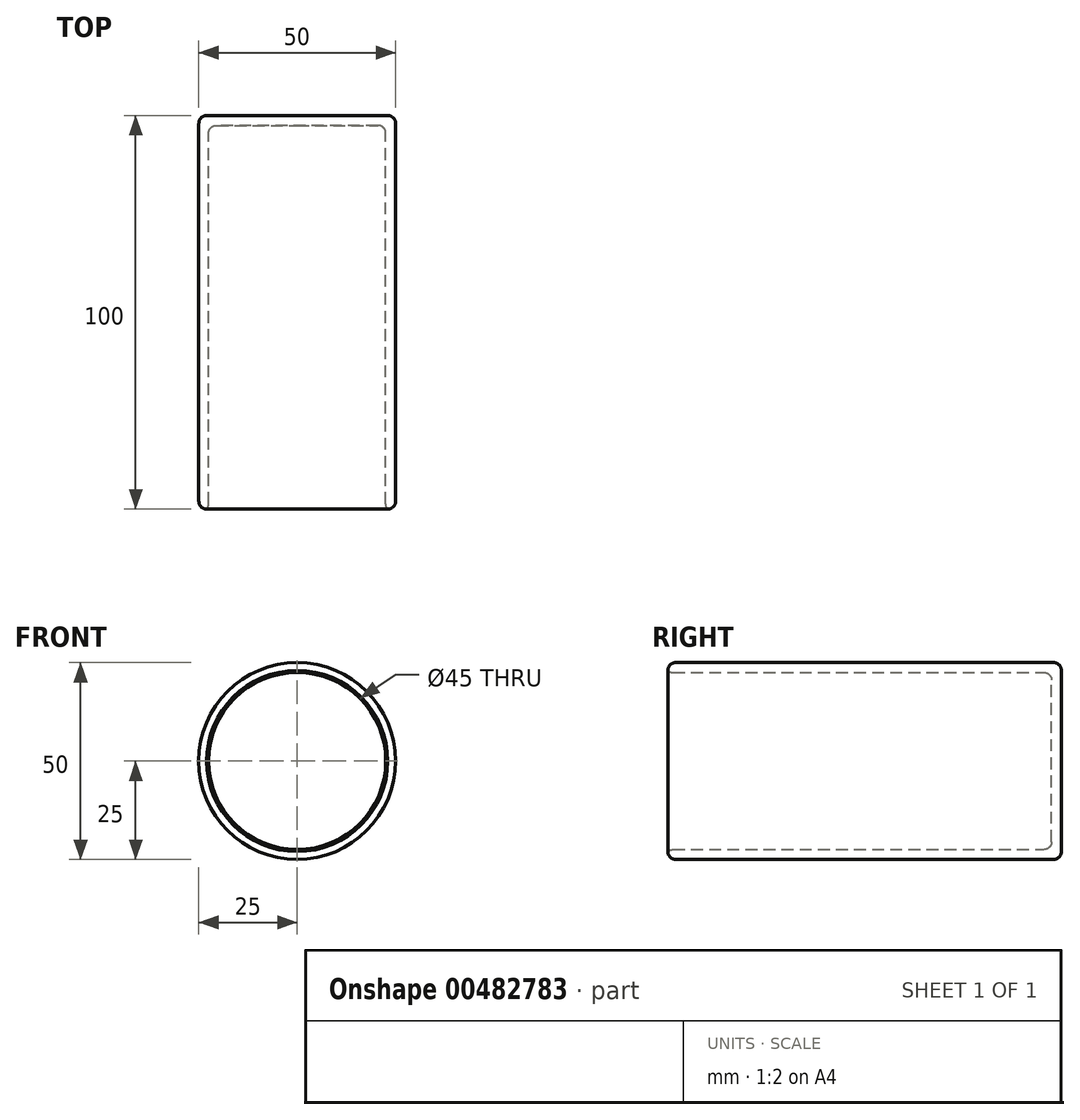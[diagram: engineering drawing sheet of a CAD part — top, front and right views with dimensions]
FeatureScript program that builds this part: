
annotation { "Feature Type Name" : "Feature", "Feature Type Description" : "" }
export const myFeature = defineFeature(function(context is Context, id is Id, definition is map)
    precondition{}
    {
        {
            var Q0;
            Q0=qCreatedBy(makeId("Front.planeOp"),FACE);
            var sketch = newSketch(context, id + "F0", { "sketchPlane" : qUnion([Q0])});
            skCircle(sketch, "E0", {"center": v(0, 0) * mm, "radius": 25 * mm});
            skSolve(sketch);
        }
        {
            var Q0;
            Q0 = qSketchRegion(id + "F0", true);
            extrude(context, id + "F1", {"entities" : qUnion([Q0]), "depth" : 100 * mm});
        }
        {
            var Q0;
            Q0=makeQuery(id+"F1.opExtrude","CAP_FACE",FACE,{"disambiguationData":[OSD([sQuery(id+"F0.wireOp",EDGE,"E0")])],"isStart":false});
            shell(context, id + "F2", {"entities" : qUnion([Q0]), "thickness" : 2.5 * mm});
        }
        {
            var Q0;
            Q0=makeQuery(id+"F1.opExtrude","SWEPT_FACE",FACE,{"disambiguationData":[OSD([sQuery(id+"F0.wireOp",EDGE,"E0")])]});
            fillet(context, id + "F3", {"entities" : qUnion([Q0]), "radius" : 2 * mm, "tangentPropagation" : true, "allowEdgeOverflow" : false});
        }
        {
            var Q0;
            {var subQ0=sQuery(id+"F0.wireOp",EDGE,"E0");Q0=makeQuery(id+"F2.opShell","OFFSET_FACE",FACE,{"disambiguationData":[OSD([subQ0]),TDD([makeQuery(id+"F1.opExtrude","SWEPT_FACE",FACE,{"disambiguationData":[OSD([subQ0])]})])]});}
            fillet(context, id + "F4", {"entities" : qUnion([Q0]), "radius" : 2 * mm, "tangentPropagation" : true, "allowEdgeOverflow" : false});
        }
    });
